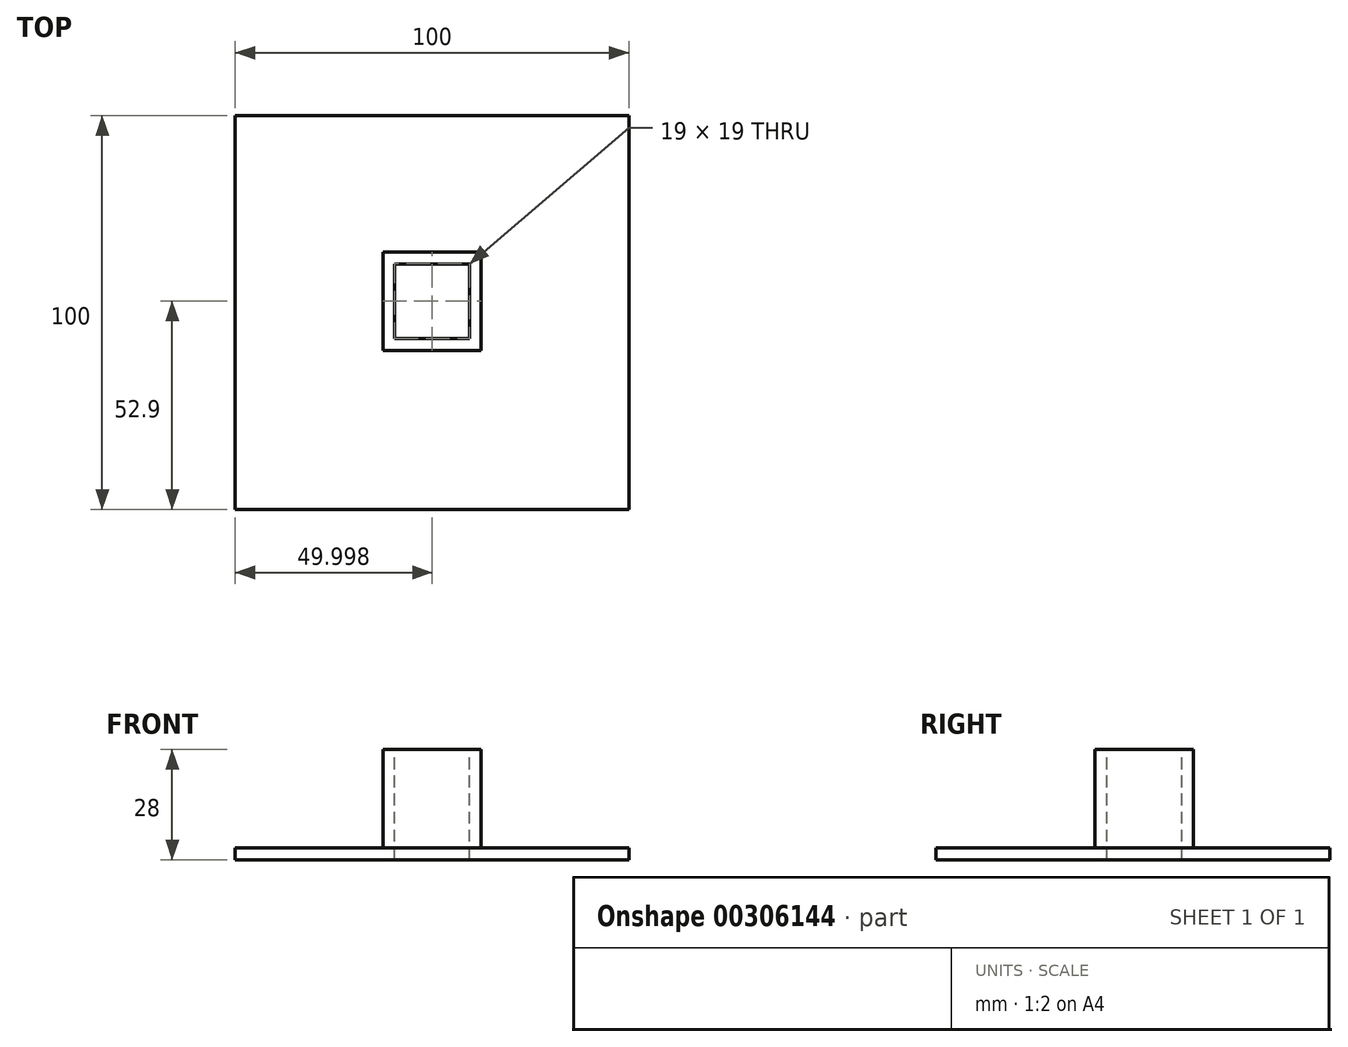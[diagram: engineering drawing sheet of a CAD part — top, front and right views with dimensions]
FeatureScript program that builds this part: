
annotation { "Feature Type Name" : "Feature", "Feature Type Description" : "" }
export const myFeature = defineFeature(function(context is Context, id is Id, definition is map)
    precondition{}
    {
        {
            var Q0;
            Q0=qCreatedBy(makeId("Top.planeOp"),FACE);
            var sketch = newSketch(context, id + "F0", { "sketchPlane" : qUnion([Q0])});
            skLineSegment(sketch, "E0.bottom", {"start": v(-51.56, 59.6) * mm, "end": v(48.44, 59.6) * mm});
            skLineSegment(sketch, "E0.top", {"start": v(-51.56, -40.4) * mm, "end": v(48.44, -40.4) * mm});
            skLineSegment(sketch, "E0.left", {"start": v(-51.56, 59.6) * mm, "end": v(-51.56, -40.4) * mm});
            skLineSegment(sketch, "E0.right", {"start": v(48.44, 59.6) * mm, "end": v(48.44, -40.4) * mm});
            skSolve(sketch);
        }
        {
            var Q0;
            Q0 = qSketchRegion(id + "F0", true);
            extrude(context, id + "F1", {"entities" : qUnion([Q0]), "depth" : 3 * mm});
        }
        {
            var Q0;
            Q0=makeQuery(id+"F1.opExtrude","CAP_FACE",FACE,{"disambiguationData":[OSD([sQuery(id+"F0.wireOp",EDGE,"E0.bottom"),sQuery(id+"F0.wireOp",EDGE,"E0.top"),sQuery(id+"F0.wireOp",EDGE,"E0.left"),sQuery(id+"F0.wireOp",EDGE,"E0.right")])],"isStart":false});
            var sketch = newSketch(context, id + "F2", { "sketchPlane" : qUnion([Q0])});
            skLineSegment(sketch, "E1.bottom", {"start": v(-14.06, 25) * mm, "end": v(10.94, 25) * mm});
            skLineSegment(sketch, "E1.top", {"start": v(-14.06, 0) * mm, "end": v(10.94, 0) * mm});
            skLineSegment(sketch, "E1.left", {"start": v(-14.06, 25) * mm, "end": v(-14.06, 0) * mm});
            skLineSegment(sketch, "E1.right", {"start": v(10.94, 25) * mm, "end": v(10.94, 0) * mm});
            skSolve(sketch);
        }
        {
            var Q0;
            Q0 = qSketchRegion(id + "F2", true);
            extrude(context, id + "F3", {"entities" : qUnion([Q0]), "operationType" : NewBodyOperationType.ADD, "depth" : 25 * mm});
        }
        {
            var Q0;
            Q0=makeQuery(id+"F3.opExtrude","CAP_FACE",FACE,{"disambiguationData":[OSD([sQuery(id+"F2.wireOp",EDGE,"E1.bottom"),sQuery(id+"F2.wireOp",EDGE,"E1.top"),sQuery(id+"F2.wireOp",EDGE,"E1.left"),sQuery(id+"F2.wireOp",EDGE,"E1.right")])],"isStart":false});
            var sketch = newSketch(context, id + "F4", { "sketchPlane" : qUnion([Q0])});
            skLineSegment(sketch, "E2.bottom", {"start": v(-11.06, 22) * mm, "end": v(7.94, 22) * mm});
            skLineSegment(sketch, "E2.top", {"start": v(-11.06, 3) * mm, "end": v(7.94, 3) * mm});
            skLineSegment(sketch, "E2.left", {"start": v(-11.06, 22) * mm, "end": v(-11.06, 3) * mm});
            skLineSegment(sketch, "E2.right", {"start": v(7.94, 22) * mm, "end": v(7.94, 3) * mm});
            skSolve(sketch);
        }
        {
            var Q0;
            Q0 = qSketchRegion(id + "F4", true);
            extrude(context, id + "F5", {"entities" : qUnion([Q0]), "operationType" : NewBodyOperationType.REMOVE, "oppositeDirection" : true, "depth" : 85.1 * mm});
        }
    });
